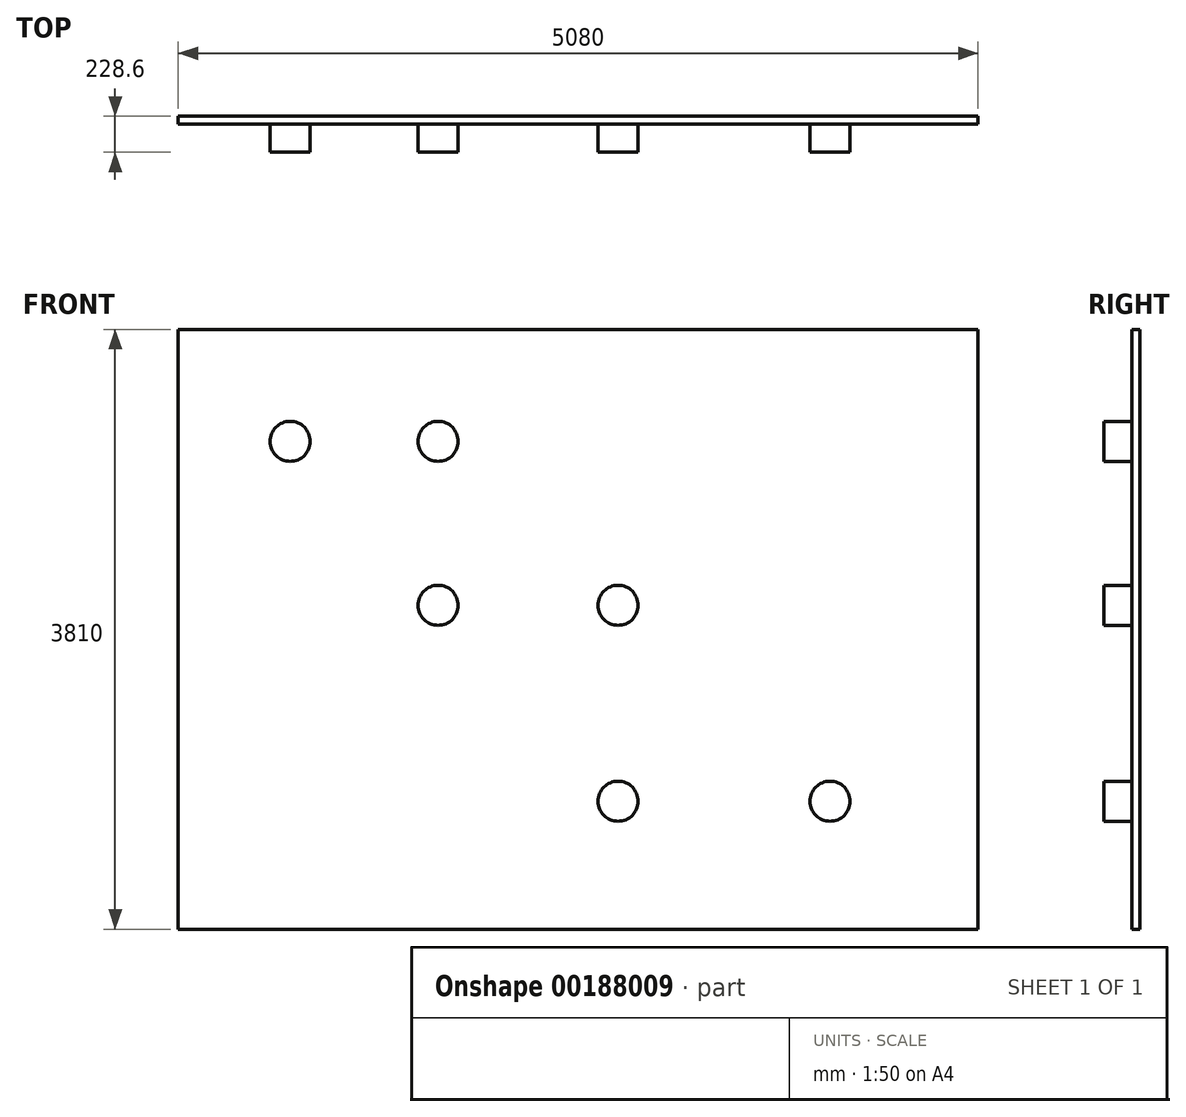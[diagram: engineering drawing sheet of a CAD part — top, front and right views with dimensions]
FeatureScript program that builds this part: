
annotation { "Feature Type Name" : "Feature", "Feature Type Description" : "" }
export const myFeature = defineFeature(function(context is Context, id is Id, definition is map)
    precondition{}
    {
        {
            var Q0;
            Q0=qCreatedBy(makeId("Front.planeOp"),FACE);
            var sketch = newSketch(context, id + "F0", { "sketchPlane" : qUnion([Q0])});
            skLineSegment(sketch, "E0.bottom", {"start": v(-126.06, 3694.01) * mm, "end": v(4953.94, 3694.01) * mm});
            skLineSegment(sketch, "E0.top", {"start": v(-126.06, -115.99) * mm, "end": v(4953.94, -115.99) * mm});
            skLineSegment(sketch, "E0.left", {"start": v(-126.06, 3694.01) * mm, "end": v(-126.06, -115.99) * mm});
            skLineSegment(sketch, "E0.right", {"start": v(4953.94, 3694.01) * mm, "end": v(4953.94, -115.99) * mm});
            skSolve(sketch);
        }
        {
            var Q0;
            Q0=makeQuery(id+"F0.imprint","IMPRINT",FACE,{"disambiguationData":[TD([[makeQuery(id+"F0.imprint","IMPRINT",EDGE,{"derivedFrom":sQuery(id+"F0.wireOp",EDGE,"E0.bottom")}),-1.0]])]});
            extrude(context, id + "F1", {"entities" : qUnion([Q0]), "depth" : 50.8 * mm});
        }
        {
            var Q0;
            Q0=makeQuery(id+"F1.opExtrude","CAP_FACE",FACE,{"disambiguationData":[OSD([sQuery(id+"F0.wireOp",EDGE,"E0.bottom"),sQuery(id+"F0.wireOp",EDGE,"E0.top"),sQuery(id+"F0.wireOp",EDGE,"E0.left"),sQuery(id+"F0.wireOp",EDGE,"E0.right")])],"isStart":false});
            var sketch = newSketch(context, id + "F2", { "sketchPlane" : qUnion([Q0])});
            skCircle(sketch, "E1", {"center": v(585.14, 2982.81) * mm, "radius": 127 * mm});
            skCircle(sketch, "E2", {"center": v(1524.94, 2982.81) * mm, "radius": 127 * mm});
            skCircle(sketch, "E3", {"center": v(1524.94, 1941.41) * mm, "radius": 127 * mm});
            skCircle(sketch, "E4", {"center": v(2667.94, 1941.41) * mm, "radius": 127 * mm});
            skCircle(sketch, "E5", {"center": v(2667.94, 696.81) * mm, "radius": 127 * mm});
            skCircle(sketch, "E6", {"center": v(4014.14, 696.81) * mm, "radius": 127 * mm});
            skSolve(sketch);
        }
        {
            var Q0;
            Q0=qSketchRegion(id+"F2",true);
            extrude(context, id + "F3", {"entities" : qUnion([Q0]), "operationType" : NewBodyOperationType.ADD, "depth" : 177.8 * mm});
        }
    });
